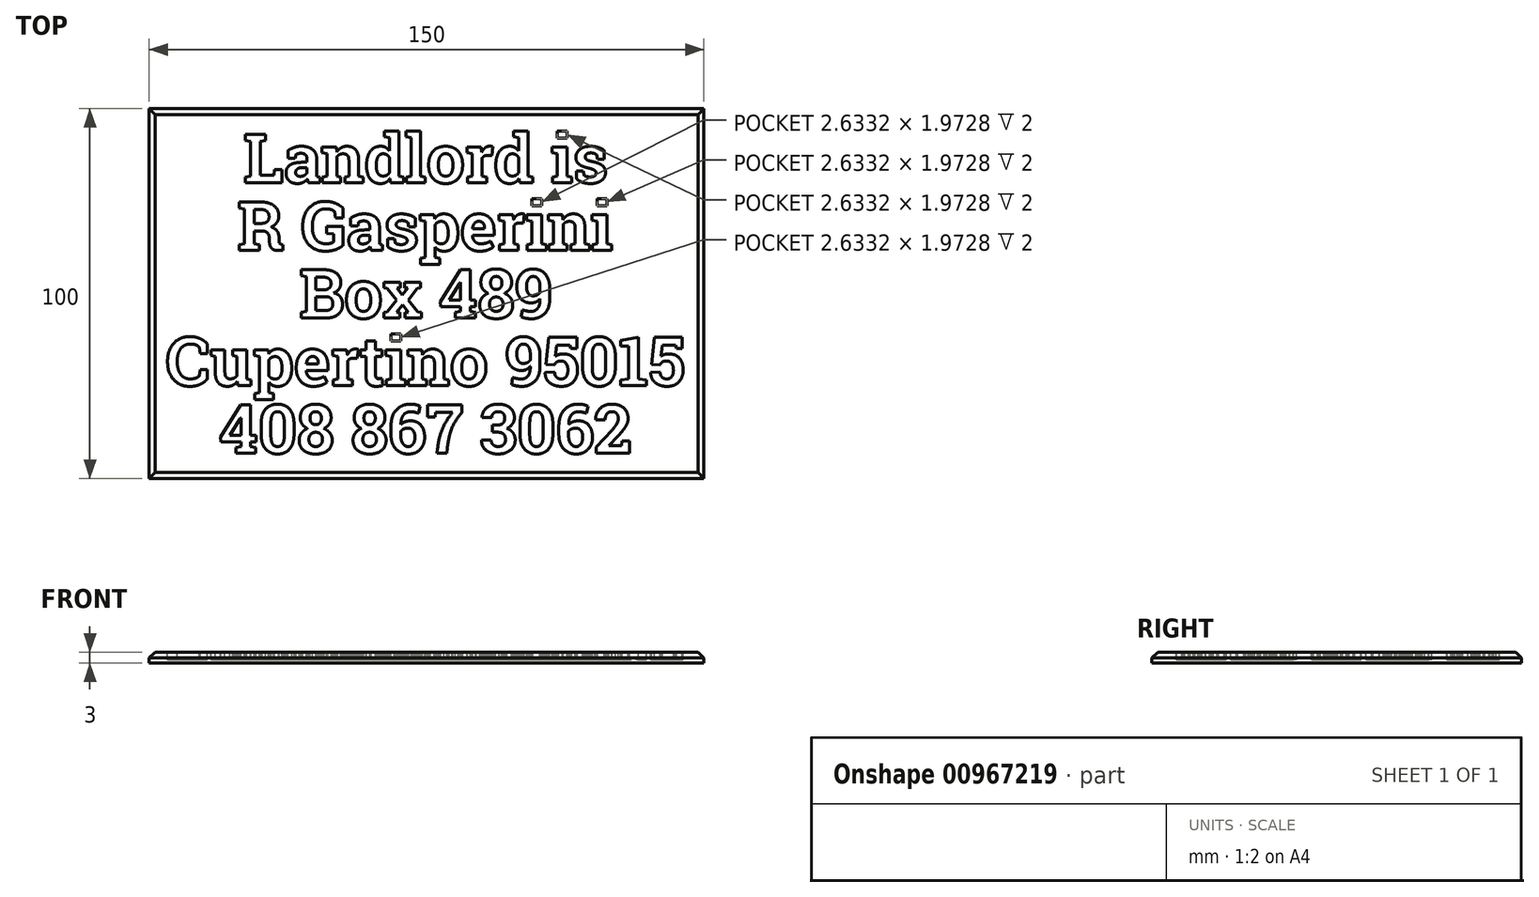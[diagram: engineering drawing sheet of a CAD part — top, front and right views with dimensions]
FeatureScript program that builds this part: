
annotation { "Feature Type Name" : "Feature", "Feature Type Description" : "" }
export const myFeature = defineFeature(function(context is Context, id is Id, definition is map)
    precondition{}
    {
        {
            assignVariable(context, id + "F0", {"name" : "PanelThickness", "anyValue" : 3});
        }
        {
            assignVariable(context, id + "F1", {"name" : "Engraving", "anyValue" : 2});
        }
        {
            var Q0;
            Q0=qCreatedBy(makeId("Top.planeOp"),FACE);
            var sketch = newSketch(context, id + "F2", { "sketchPlane" : qUnion([Q0])});
            skLineSegment(sketch, "E0.bottom", {"start": v(-75, 50) * mm, "end": v(75, 50) * mm});
            skLineSegment(sketch, "E0.top", {"start": v(-75, -50) * mm, "end": v(75, -50) * mm});
            skLineSegment(sketch, "E0.left", {"start": v(-75, 50) * mm, "end": v(-75, -50) * mm});
            skLineSegment(sketch, "E0.right", {"start": v(75, 50) * mm, "end": v(75, -50) * mm});
            skPoint(sketch, "E0.middle", {"position": v(0, 0) * mm});
            skSolve(sketch);
        }
        {
            var Q0;
            Q0 = qSketchRegion(id + "F2", true);
            extrude(context, id + "F3", {"entities" : qUnion([Q0]), "depth" : (getVariable(context, 'PanelThickness')) * mm, "offsetDistance" : 25 * mm});
        }
        {
            var Q0;
            Q0=makeQuery(id+"F3.opExtrude","CAP_FACE",FACE,{"disambiguationData":[OSD([sQuery(id+"F2.wireOp",EDGE,"E0.bottom"),sQuery(id+"F2.wireOp",EDGE,"E0.top"),sQuery(id+"F2.wireOp",EDGE,"E0.left"),sQuery(id+"F2.wireOp",EDGE,"E0.right")])],"isStart":false});
            var sketch = newSketch(context, id + "F4", { "sketchPlane" : qUnion([Q0])});
            skLineSegment(sketch, "E1.bottom", {"start": v(-72, 47) * mm, "end": v(72, 47) * mm, "construction": true});
            skLineSegment(sketch, "E1.top", {"start": v(-72, -47) * mm, "end": v(72, -47) * mm, "construction": true});
            skLineSegment(sketch, "E1.left", {"start": v(-72, 47) * mm, "end": v(-72, -47) * mm, "construction": true});
            skLineSegment(sketch, "E1.right", {"start": v(72, 47) * mm, "end": v(72, -47) * mm, "construction": true});
            skPoint(sketch, "E1.middle", {"position": v(0, 0) * mm});
            skLineSegment(sketch, "E2", {"start": v(0, 47) * mm, "end": v(0, -47) * mm, "construction": true});
            skLineSegment(sketch, "E3", {"start": v(-49.5, 29.93) * mm, "end": v(49.5, 29.93) * mm, "construction": true});
            skText(sketch, "E4", { "text": "Landlord is", "fontName": "RobotoSlab-Bold.ttf"});
            skText(sketch, "E5", { "text": "Box 489", "fontName": "RobotoSlab-Bold.ttf"});
            skLineSegment(sketch, "E6", {"start": v(-34.44, -6.64) * mm, "end": v(34.44, -6.64) * mm, "construction": true});
            skLineSegment(sketch, "E7", {"start": v(0, -6.64) * mm, "end": v(0, 6.64) * mm, "construction": true});
            skText(sketch, "E8", { "text": "R Gasperini", "fontName": "RobotoSlab-Bold.ttf"});
            skText(sketch, "E9", { "text": "Cupertino 95015", "fontName": "RobotoSlab-Bold.ttf"});
            skText(sketch, "E10", { "text": "408 867 3062", "fontName": "RobotoSlab-Bold.ttf"});
            const initialGuessF4  = {"E4": [-0.0495, 0.02993, 1, 0, 0.01329], "E5": [-0.03444, -0.00664, 1, 0, 0.01329], "E8": [-0.05113, 0.01164, 1, 0, 0.01329], "E9": [-0.0705, -0.02493, 1, 0, 0.01329], "E10": [-0.056, -0.04322, 1, 0, 0.01329]};
            skSetInitialGuess(sketch, initialGuessF4);
            skSolve(sketch);
        }
        {
            var Q0;
            Q0 = qSketchRegion(id + "F4", true);
            extrude(context, id + "F5", {"entities" : qUnion([Q0]), "operationType" : NewBodyOperationType.REMOVE, "oppositeDirection" : true, "depth" : (getVariable(context, 'Engraving')) * mm, "offsetDistance" : 25 * mm});
        }
        {
            var Q0;
            Q0=makeQuery(id+"F3.opExtrude","CAP_EDGE",EDGE,{"disambiguationData":[OSD([sQuery(id+"F2.wireOp",EDGE,"E0.bottom")])],"isStart":false});
            var Q1;
            Q1=makeQuery(id+"F3.opExtrude","CAP_EDGE",EDGE,{"disambiguationData":[OSD([sQuery(id+"F2.wireOp",EDGE,"E0.left")])],"isStart":false});
            var Q2;
            Q2=makeQuery(id+"F3.opExtrude","CAP_EDGE",EDGE,{"disambiguationData":[OSD([sQuery(id+"F2.wireOp",EDGE,"E0.top")])],"isStart":false});
            var Q3;
            Q3=makeQuery(id+"F3.opExtrude","CAP_EDGE",EDGE,{"disambiguationData":[OSD([sQuery(id+"F2.wireOp",EDGE,"E0.right")])],"isStart":false});
            chamfer(context, id + "F6", {"entities" : qUnion([Q0, Q1, Q2, Q3]), "width" : (getVariable(context, 'Engraving') - .4) * mm, "tangentPropagation" : true});
        }
    });
